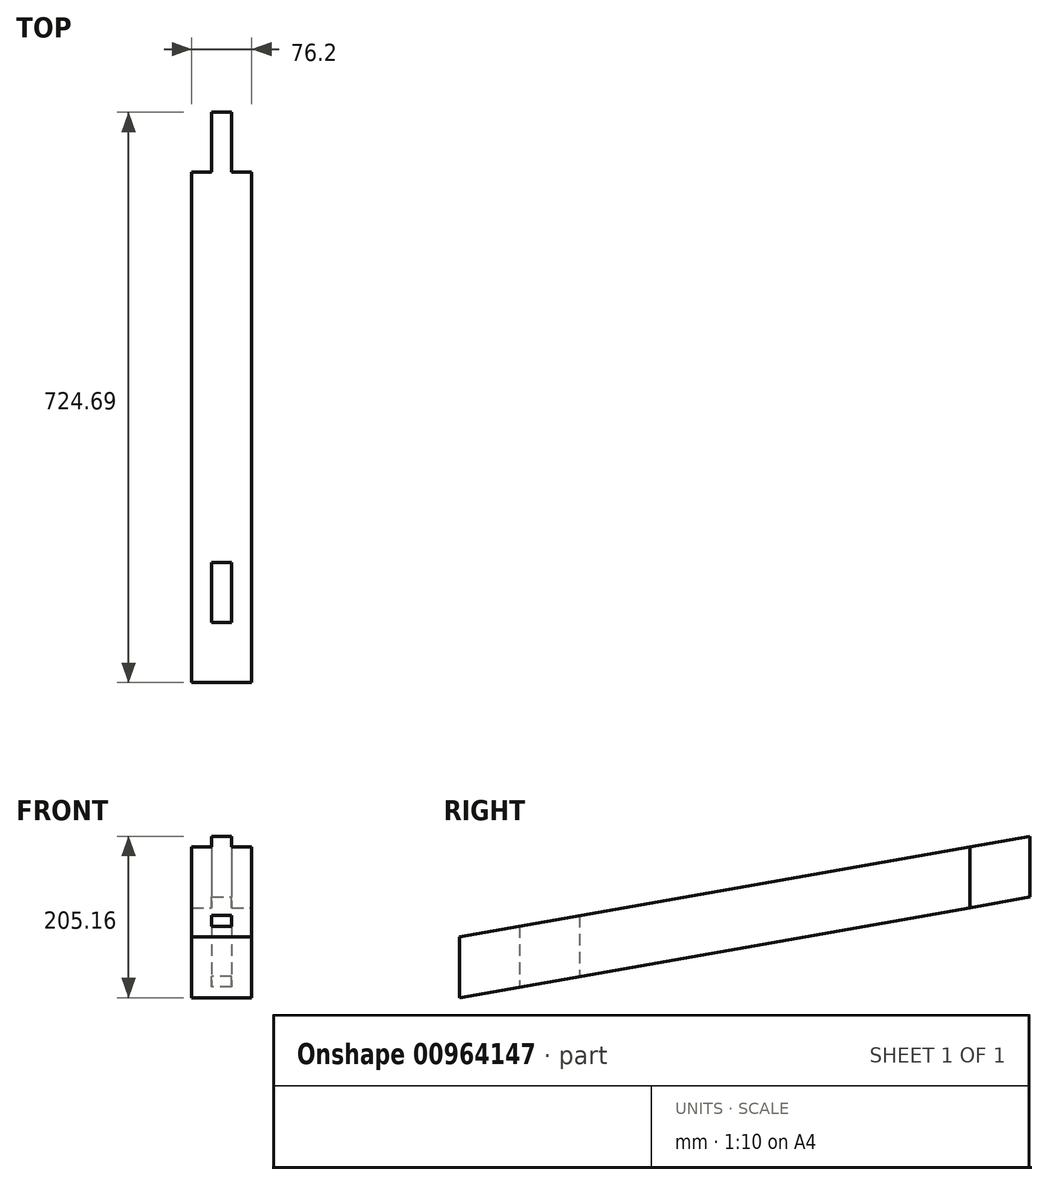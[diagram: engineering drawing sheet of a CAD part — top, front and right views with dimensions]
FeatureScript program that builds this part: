
annotation { "Feature Type Name" : "Feature", "Feature Type Description" : "" }
export const myFeature = defineFeature(function(context is Context, id is Id, definition is map)
    precondition{}
    {
        {
            var Q0;
            Q0=qCreatedBy(makeId("Top.planeOp"),FACE);
            var sketch = newSketch(context, id + "F0", { "sketchPlane" : qUnion([Q0])});
            skLineSegment(sketch, "E0", {"start": v(-71.45, -9.1) * mm, "end": v(125.71, -9.1) * mm});
            skSolve(sketch);
        }
        {
            var Q0;
            Q0=sQuery(id+"F0.wireOp",EDGE,"E0");
            var Q1;
            Q1=qCreatedBy(makeId("Origin.pointOp"),VERTEX);
            cPlane(context, id + "F1", {"entities" : qUnion([Q0, Q1]), "cplaneType" : CPlaneType.LINE_ANGLE, "offset" : 25.4 * mm, "angle" : 10 * degree, "width" : 152.4 * mm, "height" : 152.4 * mm});
        }
        {
            var Q0;
            Q0=qCreatedBy(id+"F1.planeOp",FACE);
            var sketch = newSketch(context, id + "F2", { "sketchPlane" : qUnion([Q0])});
            skLineSegment(sketch, "E1.bottom", {"start": v(-61.4, -402.2) * mm, "end": v(14.8, -402.2) * mm});
            skLineSegment(sketch, "E1.top", {"start": v(-61.4, 347.1) * mm, "end": v(14.8, 347.1) * mm});
            skLineSegment(sketch, "E1.left", {"start": v(-61.4, -402.2) * mm, "end": v(-61.4, 347.1) * mm});
            skLineSegment(sketch, "E1.right", {"start": v(14.8, -402.2) * mm, "end": v(14.8, 347.1) * mm});
            skSolve(sketch);
        }
        {
            var Q0;
            Q0=makeQuery(id+"F2.imprint","IMPRINT",FACE,{"disambiguationData":[TD([[makeQuery(id+"F2.imprint","IMPRINT",EDGE,{"derivedFrom":sQuery(id+"F2.wireOp",EDGE,"E1.bottom")}),1.0]])]});
            extrude(context, id + "F3", {"entities" : qUnion([Q0]), "depth" : 76.2 * mm, "offsetDistance" : 25.4 * mm});
        }
        {
            var Q0;
            Q0=makeQuery(id+"F3.opExtrude","CAP_EDGE",EDGE,{"disambiguationData":[OSD([sQuery(id+"F2.wireOp",EDGE,"E1.top")])],"isStart":false});
            var Q1;
            Q1=makeQuery(id+"F3.opExtrude","SWEPT_FACE",FACE,{"disambiguationData":[OSD([sQuery(id+"F2.wireOp",EDGE,"E1.top")])]});
            cPlane(context, id + "F4", {"entities" : qUnion([Q0, Q1]), "cplaneType" : CPlaneType.LINE_ANGLE, "offset" : 25.4 * mm, "angle" : 10 * degree, "oppositeDirection" : true, "width" : 152.4 * mm, "height" : 152.4 * mm});
        }
        {
            var Q0;
            Q0=qCreatedBy(id+"F4.planeOp",FACE);
            var sketch = newSketch(context, id + "F5", { "sketchPlane" : qUnion([Q0])});
            skLineSegment(sketch, "E2.bottom", {"start": v(-36, 136.87) * mm, "end": v(-61.4, 136.87) * mm});
            skLineSegment(sketch, "E2.top", {"start": v(-36, -14.06) * mm, "end": v(-61.4, -14.06) * mm});
            skLineSegment(sketch, "E2.left", {"start": v(-36, 136.87) * mm, "end": v(-36, -14.06) * mm});
            skLineSegment(sketch, "E2.right", {"start": v(-61.4, 136.87) * mm, "end": v(-61.4, -14.06) * mm});
            skLineSegment(sketch, "E3.bottom", {"start": v(-10.6, 136.87) * mm, "end": v(14.8, 136.87) * mm});
            skLineSegment(sketch, "E3.top", {"start": v(-10.6, -14.06) * mm, "end": v(14.8, -14.06) * mm});
            skLineSegment(sketch, "E3.left", {"start": v(-10.6, 136.87) * mm, "end": v(-10.6, -14.06) * mm});
            skLineSegment(sketch, "E3.right", {"start": v(14.8, 136.87) * mm, "end": v(14.8, -14.06) * mm});
            skSolve(sketch);
        }
        {
            var Q0;
            Q0 = qSketchRegion(id + "F5", true);
            extrude(context, id + "F6", {"entities" : qUnion([Q0]), "operationType" : NewBodyOperationType.REMOVE, "depth" : 76.2 * mm, "offsetDistance" : 25.4 * mm});
        }
        {
            var Q0;
            Q0=qCreatedBy(id+"F4.planeOp",FACE);
            var sketch = newSketch(context, id + "F7", { "sketchPlane" : qUnion([Q0])});
            skLineSegment(sketch, "E4.bottom", {"start": v(27.5, 149.38) * mm, "end": v(-61.4, 149.38) * mm});
            skLineSegment(sketch, "E4.top", {"start": v(27.5, 40.05) * mm, "end": v(-61.4, 40.05) * mm});
            skLineSegment(sketch, "E4.left", {"start": v(27.5, 149.38) * mm, "end": v(27.5, 40.05) * mm});
            skLineSegment(sketch, "E4.right", {"start": v(-61.4, 149.38) * mm, "end": v(-61.4, 40.05) * mm});
            skSolve(sketch);
        }
        {
            var Q0;
            Q0=makeQuery(id+"F7.imprint","IMPRINT",FACE,{"disambiguationData":[TD([[makeQuery(id+"F7.imprint","IMPRINT",EDGE,{"derivedFrom":sQuery(id+"F7.wireOp",EDGE,"E4.bottom")}),1.0]])]});
            extrude(context, id + "F8", {"entities" : qUnion([Q0]), "operationType" : NewBodyOperationType.REMOVE, "endBound" : BoundingType.THROUGH_ALL, "oppositeDirection" : true, "depth" : 25.4 * mm, "offsetDistance" : 25.4 * mm});
        }
        {
            var Q0;
            Q0=makeQuery(id+"F3.opExtrude","SWEPT_FACE",FACE,{"disambiguationData":[OSD([sQuery(id+"F2.wireOp",EDGE,"E1.bottom")])]});
            var Q1;
            Q1=makeQuery(id+"F3.opExtrude","CAP_EDGE",EDGE,{"disambiguationData":[OSD([sQuery(id+"F2.wireOp",EDGE,"E1.bottom")])],"isStart":true});
            cPlane(context, id + "F9", {"entities" : qUnion([Q0, Q1]), "cplaneType" : CPlaneType.LINE_ANGLE, "offset" : 25.4 * mm, "angle" : 10 * degree, "oppositeDirection" : true, "width" : 152.4 * mm, "height" : 152.4 * mm});
        }
        {
            var Q0;
            Q0=qCreatedBy(id+"F9.planeOp",FACE);
            var sketch = newSketch(context, id + "F10", { "sketchPlane" : qUnion([Q0])});
            skLineSegment(sketch, "E5.bottom", {"start": v(67.06, -100.05) * mm, "end": v(-54.51, -100.05) * mm});
            skLineSegment(sketch, "E5.top", {"start": v(67.06, 24.94) * mm, "end": v(-54.51, 24.94) * mm});
            skLineSegment(sketch, "E5.left", {"start": v(67.06, -100.05) * mm, "end": v(67.06, 24.94) * mm});
            skLineSegment(sketch, "E5.right", {"start": v(-54.51, -100.05) * mm, "end": v(-54.51, 24.94) * mm});
            skSolve(sketch);
        }
        {
            var Q0;
            Q0 = qSketchRegion(id + "F10", true);
            extrude(context, id + "F11", {"entities" : qUnion([Q0]), "operationType" : NewBodyOperationType.REMOVE, "oppositeDirection" : true, "depth" : 25.4 * mm, "offsetDistance" : 25.4 * mm});
        }
        {
            var Q0;
            Q0=qCreatedBy(id+"F9.planeOp",FACE);
            cPlane(context, id + "F12", {"entities" : qUnion([Q0]), "cplaneType" : CPlaneType.OFFSET, "offset" : 152.4 * mm, "width" : 152.4 * mm, "height" : 152.4 * mm});
        }
        {
            var Q0;
            Q0=qCreatedBy(id+"F12.planeOp",FACE);
            var sketch = newSketch(context, id + "F13", { "sketchPlane" : qUnion([Q0])});
            skLineSegment(sketch, "E6.bottom", {"start": v(10.6, 91.33) * mm, "end": v(36, 91.33) * mm});
            skLineSegment(sketch, "E6.top", {"start": v(10.6, -92.25) * mm, "end": v(36, -92.25) * mm});
            skLineSegment(sketch, "E6.left", {"start": v(10.6, 91.33) * mm, "end": v(10.6, -92.25) * mm});
            skLineSegment(sketch, "E6.right", {"start": v(36, 91.33) * mm, "end": v(36, -92.25) * mm});
            skSolve(sketch);
        }
        {
            var Q0;
            Q0 = qSketchRegion(id + "F13", true);
            extrude(context, id + "F14", {"entities" : qUnion([Q0]), "operationType" : NewBodyOperationType.REMOVE, "oppositeDirection" : true, "depth" : 76.2 * mm, "offsetDistance" : 25.4 * mm});
        }
    });
